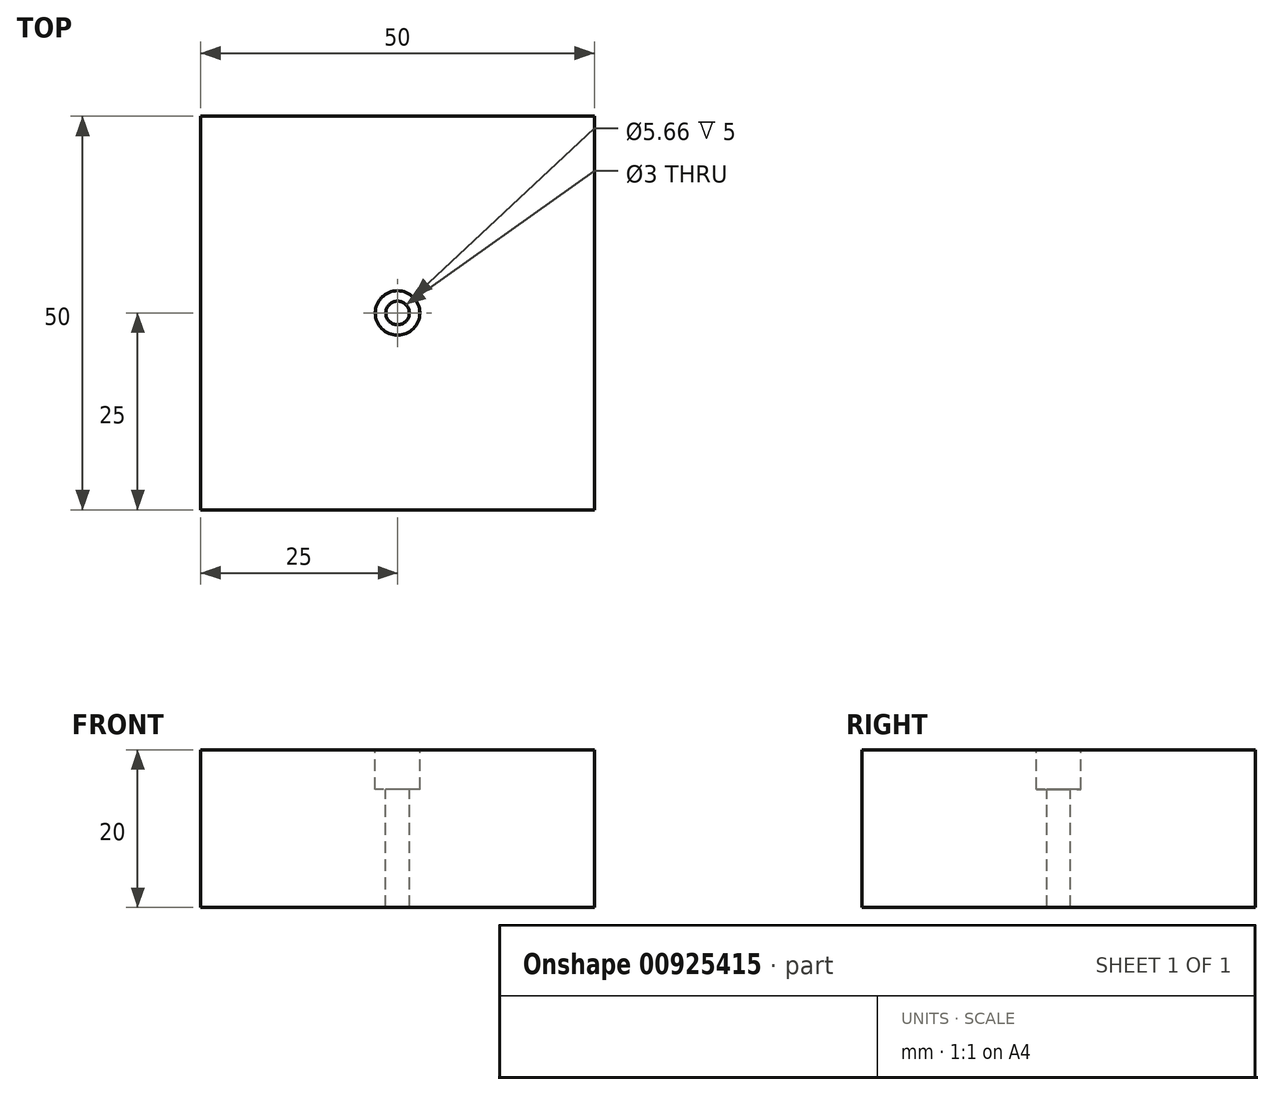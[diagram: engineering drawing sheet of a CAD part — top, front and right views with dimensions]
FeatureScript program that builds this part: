
annotation { "Feature Type Name" : "Feature", "Feature Type Description" : "" }
export const myFeature = defineFeature(function(context is Context, id is Id, definition is map)
    precondition{}
    {
        {
            var Q0;
            Q0=qCreatedBy(makeId("Top.planeOp"),FACE);
            var sketch = newSketch(context, id + "F0", { "sketchPlane" : qUnion([Q0])});
            skLineSegment(sketch, "E0.bottom", {"start": v(25, -25) * mm, "end": v(-25, -25) * mm});
            skLineSegment(sketch, "E0.top", {"start": v(25, 25) * mm, "end": v(-25, 25) * mm});
            skLineSegment(sketch, "E0.left", {"start": v(25, -25) * mm, "end": v(25, 25) * mm});
            skLineSegment(sketch, "E0.right", {"start": v(-25, -25) * mm, "end": v(-25, 25) * mm});
            skPoint(sketch, "E0.middle", {"position": v(0, 0) * mm});
            skSolve(sketch);
        }
        {
            var Q0;
            Q0 = qSketchRegion(id + "F0", true);
            extrude(context, id + "F1", {"entities" : qUnion([Q0]), "depth" : 20 * mm, "offsetDistance" : 25 * mm});
        }
        {
            var Q0;
            Q0=makeQuery(id+"F1.opExtrude","CAP_FACE",FACE,{"disambiguationData":[OSD([sQuery(id+"F0.wireOp",EDGE,"E0.bottom"),sQuery(id+"F0.wireOp",EDGE,"E0.top"),sQuery(id+"F0.wireOp",EDGE,"E0.left"),sQuery(id+"F0.wireOp",EDGE,"E0.right")])],"isStart":false});
            var sketch = newSketch(context, id + "F2", { "sketchPlane" : qUnion([Q0])});
            skLineSegment(sketch, "E1.bottom", {"start": v(2, -2) * mm, "end": v(-2, -2) * mm, "construction": true});
            skLineSegment(sketch, "E1.top", {"start": v(2, 2) * mm, "end": v(-2, 2) * mm, "construction": true});
            skLineSegment(sketch, "E1.left", {"start": v(2, -2) * mm, "end": v(2, 2) * mm, "construction": true});
            skLineSegment(sketch, "E1.right", {"start": v(-2, -2) * mm, "end": v(-2, 2) * mm, "construction": true});
            skPoint(sketch, "E1.middle", {"position": v(0, 0) * mm});
            skCircle(sketch, "E2", {"center": v(0, 0) * mm, "radius": 2.83 * mm});
            skSolve(sketch);
        }
        {
            var Q0;
            Q0 = qSketchRegion(id + "F2", true);
            extrude(context, id + "F3", {"entities" : qUnion([Q0]), "operationType" : NewBodyOperationType.REMOVE, "oppositeDirection" : true, "depth" : 5 * mm, "offsetDistance" : 25 * mm});
        }
        {
            var Q0;
            Q0=makeQuery(id+"F3.boolean.opBoolean","COPY",FACE,{"derivedFrom":makeQuery(id+"F3.opExtrude","CAP_FACE",FACE,{"disambiguationData":[OSD([sQuery(id+"F2.wireOp",EDGE,"E2")])],"isStart":false})});
            var sketch = newSketch(context, id + "F4", { "sketchPlane" : qUnion([Q0])});
            skCircle(sketch, "E3", {"center": v(0, 0) * mm, "radius": 1.5 * mm});
            skSolve(sketch);
        }
        {
            var Q0;
            Q0 = qSketchRegion(id + "F4", true);
            extrude(context, id + "F5", {"entities" : qUnion([Q0]), "operationType" : NewBodyOperationType.REMOVE, "oppositeDirection" : true, "depth" : 25 * mm, "offsetDistance" : 25 * mm});
        }
    });
